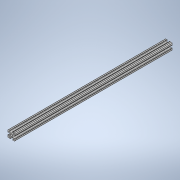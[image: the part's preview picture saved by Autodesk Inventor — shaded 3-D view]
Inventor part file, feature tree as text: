
AUTODESK INVENTOR PART (.ipt)
format: ipt  version: 2020 (Build 240168000, 168)  size: 238,080 bytes
history: native  units: in
note: dims shown in document units (in); Inventor stores cm internally (conversion verified against a paired STEP export)
features: extrude x1, sketch x1
ambient origin geometry x8: Origin, YZ Plane, XZ Plane, XY Plane, X Axis, Y Axis, Z Axis, Center Point
bodies: Solid1 (feature_tree)
feature tree (2):
  extrude  "Extrusion1"  [1 undecoded]
  sketch  "Sketch1"  dims[d0=22.0in d1=0.0in]
note: 1 required parameter value undecoded (feature->parameter linkage not recoverable at this tier; creation-order binding heuristic only, values carry confidence <= 0.55)
